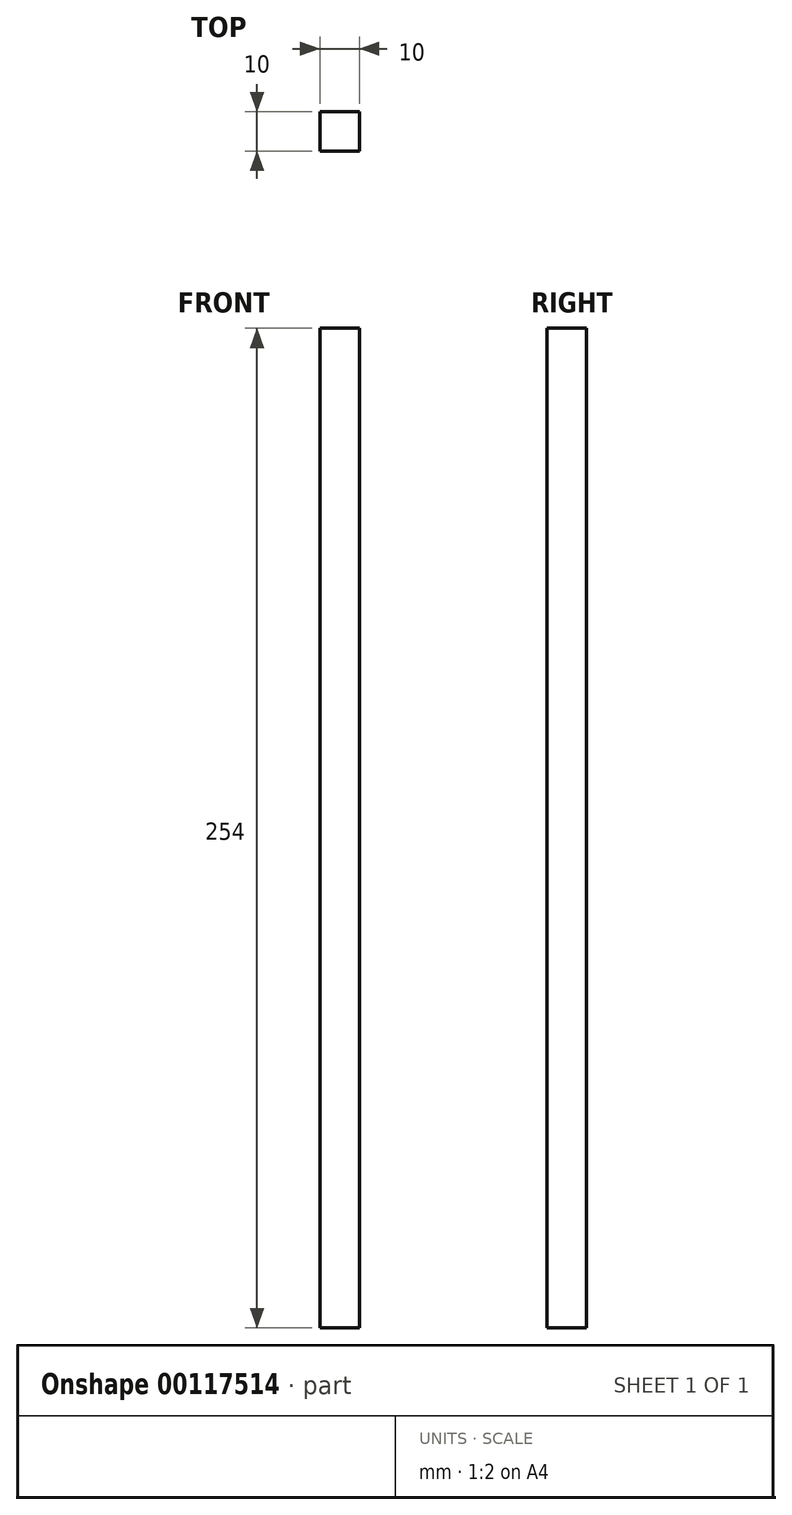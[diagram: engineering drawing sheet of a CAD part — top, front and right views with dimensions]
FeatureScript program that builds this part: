
annotation { "Feature Type Name" : "Feature", "Feature Type Description" : "" }
export const myFeature = defineFeature(function(context is Context, id is Id, definition is map)
    precondition{}
    {
        {
            var Q0;
            Q0=qCreatedBy(makeId("Top.planeOp"),FACE);
            var sketch = newSketch(context, id + "F0", { "sketchPlane" : qUnion([Q0])});
            skLineSegment(sketch, "E0.bottom", {"start": v(0, 0) * mm, "end": v(10, 0) * mm});
            skLineSegment(sketch, "E0.top", {"start": v(0, -10) * mm, "end": v(10, -10) * mm});
            skLineSegment(sketch, "E0.left", {"start": v(0, 0) * mm, "end": v(0, -10) * mm});
            skLineSegment(sketch, "E0.right", {"start": v(10, 0) * mm, "end": v(10, -10) * mm});
            skSolve(sketch);
        }
        {
            var Q0;
            Q0 = qSketchRegion(id + "F0", true);
            extrude(context, id + "F1", {"entities" : qUnion([Q0]), "depth" : 254 * mm});
        }
    });
